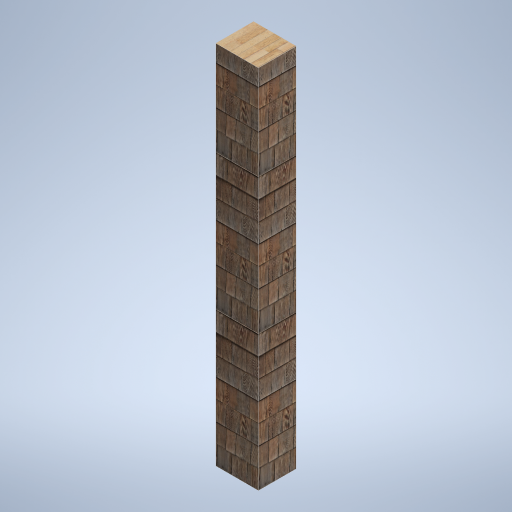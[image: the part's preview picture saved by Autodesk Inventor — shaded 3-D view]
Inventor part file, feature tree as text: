
AUTODESK INVENTOR PART (.ipt)
format: ipt  version: 2024.2 (Build 282272000, 272)  size: 346,112 bytes
history: native  units: in
note: dims shown in document units (in); Inventor stores cm internally (conversion verified against a paired STEP export)
features: other x3, sketch x1
ambient origin geometry x8: Origin, YZ Plane, XZ Plane, XY Plane, X Axis, Y Axis, Z Axis, Center Point
bodies: Solid1 (feature_tree)
feature tree (4):
  other  "support_column_01_MIR.ipt"
  other  "Solid1::support_column_01_MIR.ipt"
  other  "TaggingFeature1"
  sketch  "Sketch1"  dims[d0=0.3937in]
